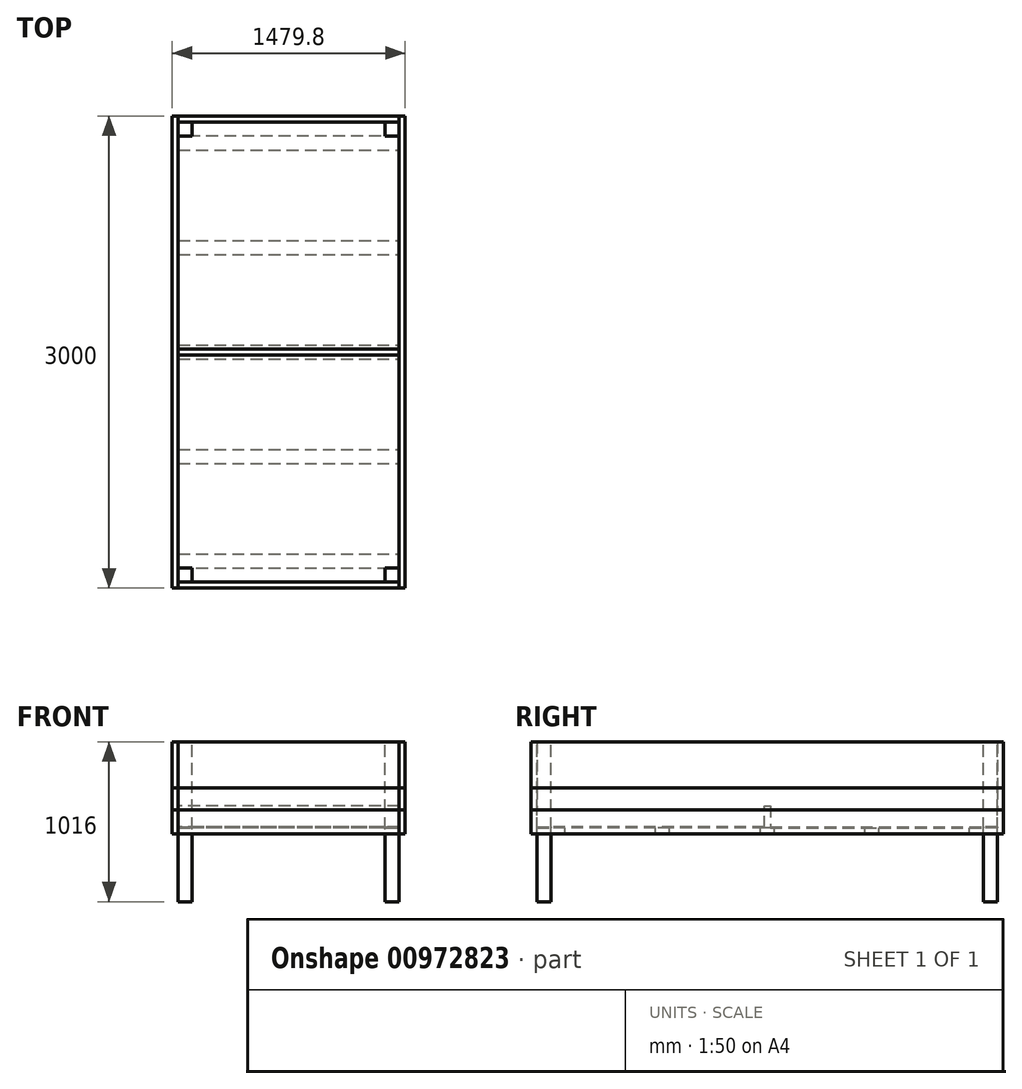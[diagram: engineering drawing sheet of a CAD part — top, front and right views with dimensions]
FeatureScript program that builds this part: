
annotation { "Feature Type Name" : "Feature", "Feature Type Description" : "" }
export const myFeature = defineFeature(function(context is Context, id is Id, definition is map)
    precondition{}
    {
        {
            var Q0;
            Q0=qCreatedBy(makeId("Top.planeOp"),FACE);
            var sketch = newSketch(context, id + "F0", { "sketchPlane" : qUnion([Q0])});
            skLineSegment(sketch, "E0.bottom", {"start": v(739.9, 1500) * mm, "end": v(-739.9, 1500) * mm});
            skLineSegment(sketch, "E0.top", {"start": v(739.9, -1500) * mm, "end": v(-739.9, -1500) * mm});
            skLineSegment(sketch, "E0.left", {"start": v(739.9, 1500) * mm, "end": v(739.9, -1500) * mm});
            skLineSegment(sketch, "E0.right", {"start": v(-739.9, 1500) * mm, "end": v(-739.9, -1500) * mm});
            skPoint(sketch, "E0.middle", {"position": v(0, 0) * mm});
            skSolve(sketch);
        }
        {
            var Q0;
            Q0=qCreatedBy(makeId("Front.planeOp"),FACE);
            var sketch = newSketch(context, id + "F1", { "sketchPlane" : qUnion([Q0])});
            skLineSegment(sketch, "E1.0", {"start": v(739.9, 0) * mm, "end": v(-739.9, 0) * mm});
            skLineSegment(sketch, "E2", {"start": v(-739.9, 0) * mm, "end": v(-739.9, -292.1) * mm});
            skLineSegment(sketch, "E3.MirrorCS", {"start": v(739.9, 0) * mm, "end": v(739.9, -292.1) * mm});
            skLineSegment(sketch, "E4", {"start": v(-739.9, -292.1) * mm, "end": v(739.9, -292.1) * mm});
            skLineSegment(sketch, "E5", {"start": v(0, 0) * mm, "end": v(0, -292.1) * mm, "construction": true});
            skLineSegment(sketch, "E6.0", {"start": v(-701.8, 0) * mm, "end": v(-701.8, -292.1) * mm});
            skLineSegment(sketch, "E7.0", {"start": v(701.8, 0) * mm, "end": v(701.8, -292.1) * mm});
            skLineSegment(sketch, "E8", {"start": v(0, 0) * mm, "end": v(0, -1016) * mm, "construction": true});
            skLineSegment(sketch, "E9", {"start": v(-739.9, -292.1) * mm, "end": v(0, -1016) * mm, "construction": true});
            skLineSegment(sketch, "E10", {"start": v(0, -1016) * mm, "end": v(-739.9, -1016) * mm, "construction": true});
            skLineSegment(sketch, "E11", {"start": v(-739.9, -1016) * mm, "end": v(-739.9, -292.1) * mm, "construction": true});
            skLineSegment(sketch, "E12", {"start": v(-739.9, -292.1) * mm, "end": v(-739.9, -431.8) * mm});
            skLineSegment(sketch, "E13", {"start": v(-739.9, -431.8) * mm, "end": v(-701.8, -431.8) * mm});
            skLineSegment(sketch, "E14", {"start": v(-701.8, -431.8) * mm, "end": v(-701.8, -292.1) * mm});
            skLineSegment(sketch, "E15.MirrorCS", {"start": v(739.9, -431.8) * mm, "end": v(701.8, -431.8) * mm});
            skLineSegment(sketch, "E16.MirrorCS", {"start": v(701.8, -431.8) * mm, "end": v(701.8, -292.1) * mm});
            skLineSegment(sketch, "E17.MirrorCS", {"start": v(739.9, -292.1) * mm, "end": v(739.9, -431.8) * mm});
            skSolve(sketch);
        }
        {
            var Q0;
            Q0=qCreatedBy(makeId("Front.planeOp"),FACE);
            var sketch = newSketch(context, id + "F2", { "sketchPlane" : qUnion([Q0])});
            skLineSegment(sketch, "E18.0", {"start": v(739.9, 0) * mm, "end": v(-739.9, 0) * mm, "construction": true});
            skLineSegment(sketch, "E19.0", {"start": v(-739.9, 0) * mm, "end": v(-739.9, -292.1) * mm, "construction": true});
            skLineSegment(sketch, "E20.0", {"start": v(-701.8, 0) * mm, "end": v(-701.8, -292.1) * mm, "construction": true});
            skLineSegment(sketch, "E21", {"start": v(-739.9, 0) * mm, "end": v(-739.9, 30) * mm});
            skLineSegment(sketch, "E22", {"start": v(-739.9, 30) * mm, "end": v(739.9, 30) * mm});
            skLineSegment(sketch, "E23", {"start": v(739.9, 30) * mm, "end": v(739.9, 0) * mm});
            skSolve(sketch);
        }
        {
            var Q0;
            {var subQ0=sQuery(id+"F1.wireOp",EDGE,"E2");Q0=makeQuery(id+"F1.imprint","IMPRINT",FACE,{"disambiguationData":[TD([[makeQuery(id+"F1.imprint","IMPRINT",EDGE,{"derivedFrom":subQ0}),1.0]])]});}
            var Q1;
            {var subQ0=sQuery(id+"F1.wireOp",EDGE,"E3.MirrorCS");Q1=makeQuery(id+"F1.imprint","IMPRINT",FACE,{"disambiguationData":[TD([[makeQuery(id+"F1.imprint","IMPRINT",EDGE,{"derivedFrom":subQ0}),-1.0]])]});}
            var Q2;
            Q2=sQuery(id+"F0.wireOp",VERTEX,"E0.top.end");
            var Q3;
            Q3=sQuery(id+"F0.wireOp",VERTEX,"E0.bottom.end");
            extrude(context, id + "F3", {"entities" : qUnion([Q0, Q1]), "endBound" : BoundingType.UP_TO_VERTEX, "depth" : 25 * mm, "endBoundEntityVertex" : qUnion([Q2]), "offsetDistance" : 25 * mm, "hasSecondDirection" : true, "secondDirectionBound" : SecondDirectionBoundingType.UP_TO_VERTEX, "secondDirectionOppositeDirection" : true, "secondDirectionDepth" : 25 * mm, "secondDirectionBoundEntityVertex" : qUnion([Q3])});
        }
        {
            var Q0;
            {var subQ0=sQuery(id+"F1.wireOp",EDGE,"E12");Q0=makeQuery(id+"F1.imprint","IMPRINT",FACE,{"disambiguationData":[TD([[makeQuery(id+"F1.imprint","IMPRINT",EDGE,{"derivedFrom":subQ0}),1.0]])]});}
            var Q1;
            Q1=makeQuery(id+"F1.imprint","IMPRINT",FACE,{"disambiguationData":[TD([[makeQuery(id+"F1.imprint","IMPRINT",EDGE,{"derivedFrom":sQuery(id+"F1.wireOp",EDGE,"E15.MirrorCS")}),-1.0]])]});
            var Q2;
            Q2=makeQuery(id+"F3.opExtrude","CAP_FACE",FACE,{"disambiguationData":[OSD([sQuery(id+"F1.wireOp",EDGE,"E1.0"),sQuery(id+"F1.wireOp",EDGE,"E2"),sQuery(id+"F1.wireOp",EDGE,"E4"),sQuery(id+"F1.wireOp",EDGE,"E6.0")])],"isStart":false});
            var Q3;
            Q3=makeQuery(id+"F3.opExtrude","CAP_FACE",FACE,{"disambiguationData":[OSD([sQuery(id+"F1.wireOp",EDGE,"E1.0"),sQuery(id+"F1.wireOp",EDGE,"E3.MirrorCS"),sQuery(id+"F1.wireOp",EDGE,"E4"),sQuery(id+"F1.wireOp",EDGE,"E7.0")])],"isStart":true});
            extrude(context, id + "F4", {"entities" : qUnion([Q0, Q1]), "endBound" : BoundingType.UP_TO_SURFACE, "depth" : 25 * mm, "endBoundEntityFace" : qUnion([Q2]), "offsetDistance" : 25 * mm, "hasSecondDirection" : true, "secondDirectionBound" : SecondDirectionBoundingType.UP_TO_SURFACE, "secondDirectionOppositeDirection" : true, "secondDirectionDepth" : 25 * mm, "secondDirectionBoundEntityFace" : qUnion([Q3])});
        }
        {
            var Q0;
            Q0=qCreatedBy(makeId("Right.planeOp"),FACE);
            var sketch = newSketch(context, id + "F5", { "sketchPlane" : qUnion([Q0])});
            skLineSegment(sketch, "E24", {"start": v(-1500, 0) * mm, "end": v(-1461.9, 0) * mm});
            skLineSegment(sketch, "E25", {"start": v(-1461.9, 0) * mm, "end": v(-1461.9, -292.1) * mm});
            skLineSegment(sketch, "E26", {"start": v(-1500, 0) * mm, "end": v(-1500, -292.1) * mm});
            skLineSegment(sketch, "E27", {"start": v(-1500, -292.1) * mm, "end": v(-1461.9, -292.1) * mm});
            skLineSegment(sketch, "E28.MirrorCS", {"start": v(1500, 0) * mm, "end": v(1461.9, 0) * mm});
            skLineSegment(sketch, "E29.MirrorCS", {"start": v(1500, -292.1) * mm, "end": v(1461.9, -292.1) * mm});
            skLineSegment(sketch, "E30.MirrorCS", {"start": v(1500, 0) * mm, "end": v(1500, -292.1) * mm});
            skLineSegment(sketch, "E31.MirrorCS", {"start": v(1461.9, 0) * mm, "end": v(1461.9, -292.1) * mm});
            skLineSegment(sketch, "E32", {"start": v(-1500, -292.1) * mm, "end": v(-1500, -431.8) * mm});
            skLineSegment(sketch, "E33", {"start": v(-1500, -431.8) * mm, "end": v(-1461.9, -431.8) * mm});
            skLineSegment(sketch, "E34", {"start": v(-1461.9, -431.8) * mm, "end": v(-1461.9, -292.1) * mm});
            skLineSegment(sketch, "E35.MirrorCS", {"start": v(1500, -431.8) * mm, "end": v(1461.9, -431.8) * mm});
            skLineSegment(sketch, "E36.MirrorCS", {"start": v(1461.9, -431.8) * mm, "end": v(1461.9, -292.1) * mm});
            skLineSegment(sketch, "E37.MirrorCS", {"start": v(1500, -292.1) * mm, "end": v(1500, -431.8) * mm});
            skLineSegment(sketch, "E38.0", {"start": v(-1500, -292.1) * mm, "end": v(1500, -292.1) * mm, "construction": true});
            skLineSegment(sketch, "E39.0", {"start": v(-1500, -431.8) * mm, "end": v(1500, -431.8) * mm, "construction": true});
            skLineSegment(sketch, "E40.0", {"start": v(0, -292.1) * mm, "end": v(0, -431.8) * mm, "construction": true});
            skLineSegment(sketch, "E41", {"start": v(0, -292.1) * mm, "end": v(-19.05, -292.1) * mm});
            skLineSegment(sketch, "E42", {"start": v(-19.05, -292.1) * mm, "end": v(-19.05, -431.8) * mm});
            skLineSegment(sketch, "E43", {"start": v(-19.05, -431.8) * mm, "end": v(19.05, -431.8) * mm});
            skLineSegment(sketch, "E44", {"start": v(19.05, -431.8) * mm, "end": v(19.05, -292.1) * mm});
            skLineSegment(sketch, "E45", {"start": v(19.05, -292.1) * mm, "end": v(0, -292.1) * mm});
            skSolve(sketch);
        }
        {
            var Q0;
            Q0=makeQuery(id+"F5.imprint","IMPRINT",FACE,{"disambiguationData":[TD([[makeQuery(id+"F5.imprint","IMPRINT",EDGE,{"derivedFrom":sQuery(id+"F5.wireOp",EDGE,"E28.MirrorCS")}),1.0]])]});
            var Q1;
            Q1=makeQuery(id+"F5.imprint","IMPRINT",FACE,{"disambiguationData":[TD([[makeQuery(id+"F5.imprint","IMPRINT",EDGE,{"derivedFrom":sQuery(id+"F5.wireOp",EDGE,"E24")}),-1.0]])]});
            var Q2;
            Q2=makeQuery(id+"F3.opExtrude","SWEPT_FACE",FACE,{"disambiguationData":[OSD([sQuery(id+"F1.wireOp",EDGE,"E7.0")])]});
            var Q3;
            Q3=makeQuery(id+"F3.opExtrude","SWEPT_FACE",FACE,{"disambiguationData":[OSD([sQuery(id+"F1.wireOp",EDGE,"E6.0")])]});
            extrude(context, id + "F6", {"entities" : qUnion([Q0, Q1]), "endBound" : BoundingType.UP_TO_SURFACE, "depth" : 25 * mm, "endBoundEntityFace" : qUnion([Q2]), "offsetDistance" : 25 * mm, "hasSecondDirection" : true, "secondDirectionBound" : SecondDirectionBoundingType.UP_TO_SURFACE, "secondDirectionOppositeDirection" : true, "secondDirectionDepth" : 25 * mm, "secondDirectionBoundEntityFace" : qUnion([Q3])});
        }
        {
            var Q0;
            Q0=makeQuery(id+"F5.imprint","IMPRINT",FACE,{"disambiguationData":[TD([[makeQuery(id+"F5.imprint","IMPRINT",EDGE,{"derivedFrom":sQuery(id+"F5.wireOp",EDGE,"E27")}),-1.0]])]});
            var Q1;
            Q1=makeQuery(id+"F5.imprint","IMPRINT",FACE,{"disambiguationData":[TD([[makeQuery(id+"F5.imprint","IMPRINT",EDGE,{"derivedFrom":sQuery(id+"F5.wireOp",EDGE,"E29.MirrorCS")}),1.0]])]});
            var Q2;
            Q2=makeQuery(id+"F5.imprint","IMPRINT",FACE,{"disambiguationData":[TD([[makeQuery(id+"F5.imprint","IMPRINT",EDGE,{"derivedFrom":sQuery(id+"F5.wireOp",EDGE,"E41")}),1.0]])]});
            var Q3;
            Q3=makeQuery(id+"F4.opExtrude","SWEPT_FACE",FACE,{"disambiguationData":[OSD([sQuery(id+"F1.wireOp",EDGE,"E16.MirrorCS")])]});
            var Q4;
            Q4=makeQuery(id+"F4.opExtrude","SWEPT_FACE",FACE,{"disambiguationData":[OSD([sQuery(id+"F1.wireOp",EDGE,"E14")])]});
            extrude(context, id + "F7", {"entities" : qUnion([Q0, Q1, Q2]), "endBound" : BoundingType.UP_TO_SURFACE, "depth" : 25 * mm, "endBoundEntityFace" : qUnion([Q3]), "offsetDistance" : 25 * mm, "hasSecondDirection" : true, "secondDirectionBound" : SecondDirectionBoundingType.UP_TO_SURFACE, "secondDirectionOppositeDirection" : true, "secondDirectionDepth" : 25 * mm, "secondDirectionBoundEntityFace" : qUnion([Q4])});
        }
        {
            var Q0;
            Q0=qCreatedBy(makeId("Top.planeOp"),FACE);
            var sketch = newSketch(context, id + "F8", { "sketchPlane" : qUnion([Q0])});
            skLineSegment(sketch, "E46.0", {"start": v(-701.8, -1500) * mm, "end": v(-701.8, 1500) * mm});
            skLineSegment(sketch, "E47.0", {"start": v(701.8, 1461.9) * mm, "end": v(-701.8, 1461.9) * mm});
            skLineSegment(sketch, "E48.0", {"start": v(-739.9, 0) * mm, "end": v(739.9, 0) * mm});
            skLineSegment(sketch, "E49", {"start": v(0, 0) * mm, "end": v(0, 1461.9) * mm, "construction": true});
            skLineSegment(sketch, "E50.bottom", {"start": v(-701.8, 1461.9) * mm, "end": v(-612.9, 1461.9) * mm});
            skLineSegment(sketch, "E50.top", {"start": v(-701.8, 1373) * mm, "end": v(-612.9, 1373) * mm});
            skLineSegment(sketch, "E50.left", {"start": v(-701.8, 1461.9) * mm, "end": v(-701.8, 1373) * mm});
            skLineSegment(sketch, "E50.right", {"start": v(-612.9, 1461.9) * mm, "end": v(-612.9, 1373) * mm});
            skLineSegment(sketch, "E51.MirrorCS", {"start": v(701.8, 1373) * mm, "end": v(612.9, 1373) * mm});
            skLineSegment(sketch, "E52.MirrorCS", {"start": v(701.8, 1461.9) * mm, "end": v(612.9, 1461.9) * mm});
            skLineSegment(sketch, "E53.MirrorCS", {"start": v(612.9, 1461.9) * mm, "end": v(612.9, 1373) * mm});
            skLineSegment(sketch, "E54.MirrorCS", {"start": v(701.8, 1461.9) * mm, "end": v(701.8, 1373) * mm});
            skLineSegment(sketch, "E55.MirrorCS", {"start": v(612.9, -1461.9) * mm, "end": v(612.9, -1373) * mm});
            skLineSegment(sketch, "E56.MirrorCS", {"start": v(701.8, -1461.9) * mm, "end": v(701.8, -1373) * mm});
            skLineSegment(sketch, "E57.MirrorCS", {"start": v(701.8, -1461.9) * mm, "end": v(612.9, -1461.9) * mm});
            skLineSegment(sketch, "E58.MirrorCS", {"start": v(701.8, -1373) * mm, "end": v(612.9, -1373) * mm});
            skLineSegment(sketch, "E59.MirrorCS", {"start": v(-612.9, -1461.9) * mm, "end": v(-612.9, -1373) * mm});
            skLineSegment(sketch, "E60.MirrorCS", {"start": v(-701.8, -1461.9) * mm, "end": v(-701.8, -1373) * mm});
            skLineSegment(sketch, "E61.MirrorCS", {"start": v(-701.8, -1373) * mm, "end": v(-612.9, -1373) * mm});
            skLineSegment(sketch, "E62.MirrorCS", {"start": v(-701.8, -1461.9) * mm, "end": v(-612.9, -1461.9) * mm});
            skSolve(sketch);
        }
        {
            var Q0;
            Q0=sQuery(id+"F1.wireOp",EDGE,"E10");
            cPlane(context, id + "F9", {"entities" : qUnion([Q0]), "cplaneType" : CPlaneType.LINE_ANGLE, "offset" : 25 * mm, "angle" : 90 * degree, "width" : 150 * mm, "height" : 150 * mm});
        }
        {
            var Q0;
            Q0=makeQuery(id+"F8.imprint","IMPRINT",FACE,{"disambiguationData":[TD([[makeQuery(id+"F8.imprint","IMPRINT",EDGE,{"derivedFrom":sQuery(id+"F8.wireOp",EDGE,"E50.bottom")}),-1.0]])]});
            var Q1;
            Q1=makeQuery(id+"F8.imprint","IMPRINT",FACE,{"disambiguationData":[TD([[makeQuery(id+"F8.imprint","IMPRINT",EDGE,{"derivedFrom":sQuery(id+"F8.wireOp",EDGE,"E51.MirrorCS")}),-1.0]])]});
            var Q2;
            Q2=makeQuery(id+"F8.imprint","IMPRINT",FACE,{"disambiguationData":[TD([[makeQuery(id+"F8.imprint","IMPRINT",EDGE,{"derivedFrom":sQuery(id+"F8.wireOp",EDGE,"E59.MirrorCS")}),1.0]])]});
            var Q3;
            Q3=makeQuery(id+"F8.imprint","IMPRINT",FACE,{"disambiguationData":[TD([[makeQuery(id+"F8.imprint","IMPRINT",EDGE,{"derivedFrom":sQuery(id+"F8.wireOp",EDGE,"E55.MirrorCS")}),-1.0]])]});
            var Q4;
            Q4=qCreatedBy(id+"F9.planeOp",FACE);
            extrude(context, id + "F10", {"entities" : qUnion([Q0, Q1, Q2, Q3]), "endBound" : BoundingType.UP_TO_SURFACE, "oppositeDirection" : true, "depth" : 40 * mm, "endBoundEntityFace" : qUnion([Q4]), "offsetDistance" : 25 * mm});
        }
        {
            var Q0;
            Q0=makeQuery(id+"F7.opExtrude","SWEPT_FACE",FACE,{"disambiguationData":[OSD([sQuery(id+"F5.wireOp",EDGE,"E33")])]});
            cPlane(context, id + "F11", {"entities" : qUnion([Q0]), "cplaneType" : CPlaneType.OFFSET, "offset" : 114.3 * mm, "width" : 152.4 * mm, "height" : 152.4 * mm});
        }
        {
            var Q0;
            Q0=qCreatedBy(id+"F11.planeOp",FACE);
            var sketch = newSketch(context, id + "F12", { "sketchPlane" : qUnion([Q0])});
            skLineSegment(sketch, "E63.0.0", {"start": v(-612.9, 1373) * mm, "end": v(-612.9, 1461.9) * mm});
            skLineSegment(sketch, "E63.0.1", {"start": v(-612.9, 1461.9) * mm, "end": v(-701.8, 1461.9) * mm});
            skLineSegment(sketch, "E63.0.2", {"start": v(-701.8, 1461.9) * mm, "end": v(-701.8, 1373) * mm});
            skLineSegment(sketch, "E63.0.3", {"start": v(-701.8, 1373) * mm, "end": v(-612.9, 1373) * mm});
            skLineSegment(sketch, "E64.0.0", {"start": v(612.9, 1461.9) * mm, "end": v(612.9, 1373) * mm});
            skLineSegment(sketch, "E64.0.1", {"start": v(612.9, 1373) * mm, "end": v(701.8, 1373) * mm});
            skLineSegment(sketch, "E64.0.2", {"start": v(701.8, 1373) * mm, "end": v(701.8, 1461.9) * mm});
            skLineSegment(sketch, "E64.0.3", {"start": v(701.8, 1461.9) * mm, "end": v(612.9, 1461.9) * mm});
            skLineSegment(sketch, "E65.0.0", {"start": v(-612.9, -1461.9) * mm, "end": v(-612.9, -1373) * mm});
            skLineSegment(sketch, "E65.0.1", {"start": v(-612.9, -1373) * mm, "end": v(-701.8, -1373) * mm});
            skLineSegment(sketch, "E65.0.2", {"start": v(-701.8, -1373) * mm, "end": v(-701.8, -1461.9) * mm});
            skLineSegment(sketch, "E65.0.3", {"start": v(-701.8, -1461.9) * mm, "end": v(-612.9, -1461.9) * mm});
            skLineSegment(sketch, "E66.0.0", {"start": v(612.9, -1461.9) * mm, "end": v(701.8, -1461.9) * mm});
            skLineSegment(sketch, "E66.0.1", {"start": v(701.8, -1461.9) * mm, "end": v(701.8, -1373) * mm});
            skLineSegment(sketch, "E66.0.2", {"start": v(701.8, -1373) * mm, "end": v(612.9, -1373) * mm});
            skLineSegment(sketch, "E66.0.3", {"start": v(612.9, -1373) * mm, "end": v(612.9, -1461.9) * mm});
            skLineSegment(sketch, "E67.0", {"start": v(701.8, -1461.9) * mm, "end": v(-701.8, -1461.9) * mm});
            skLineSegment(sketch, "E68.0", {"start": v(-701.8, 1500) * mm, "end": v(-701.8, 1373) * mm});
            skLineSegment(sketch, "E69.0", {"start": v(701.8, 1500) * mm, "end": v(701.8, 1373) * mm});
            skLineSegment(sketch, "E70.0", {"start": v(701.8, 1461.9) * mm, "end": v(-701.8, 1461.9) * mm});
            skLineSegment(sketch, "E71.0", {"start": v(701.8, 19.05) * mm, "end": v(-701.8, 19.05) * mm});
            skLineSegment(sketch, "E72.0", {"start": v(701.8, -19.05) * mm, "end": v(-701.8, -19.05) * mm});
            skLineSegment(sketch, "E73", {"start": v(-701.8, -1373) * mm, "end": v(701.8, -1373) * mm});
            skLineSegment(sketch, "E74.0", {"start": v(-739.9, 1500) * mm, "end": v(-739.9, -1500) * mm});
            skLineSegment(sketch, "E75.0", {"start": v(739.9, 1500) * mm, "end": v(739.9, -1500) * mm});
            skLineSegment(sketch, "E76", {"start": v(-739.9, 1373) * mm, "end": v(-701.8, 1373) * mm, "construction": true});
            skLineSegment(sketch, "E77", {"start": v(701.8, 1373) * mm, "end": v(739.9, 1373) * mm, "construction": true});
            skLineSegment(sketch, "E78", {"start": v(701.8, -1373) * mm, "end": v(739.9, -1373) * mm, "construction": true});
            skLineSegment(sketch, "E79", {"start": v(-701.8, -1373) * mm, "end": v(-739.9, -1373) * mm, "construction": true});
            skLineSegment(sketch, "E80", {"start": v(-739.9, 1373) * mm, "end": v(739.9, 1373) * mm});
            skLineSegment(sketch, "E81", {"start": v(-739.9, 1373) * mm, "end": v(-739.9, 1284.1) * mm});
            skLineSegment(sketch, "E82", {"start": v(-739.9, 1284.1) * mm, "end": v(739.9, 1284.1) * mm});
            skLineSegment(sketch, "E83", {"start": v(739.9, 1284.1) * mm, "end": v(739.9, 1373) * mm});
            skLineSegment(sketch, "E84.trimOffspring", {"start": v(-701.8, 1284.1) * mm, "end": v(-701.8, 708.72) * mm});
            skLineSegment(sketch, "E85.trimOffspring", {"start": v(701.8, 1284.1) * mm, "end": v(701.8, 708.72) * mm});
            skLineSegment(sketch, "E86.MirrorCS", {"start": v(-739.9, -1373) * mm, "end": v(739.9, -1373) * mm});
            skLineSegment(sketch, "E87.MirrorCS", {"start": v(-739.9, -1284.1) * mm, "end": v(739.9, -1284.1) * mm});
            skLineSegment(sketch, "E88.MirrorCS", {"start": v(739.9, -1284.1) * mm, "end": v(739.9, -1373) * mm});
            skLineSegment(sketch, "E89.MirrorCS", {"start": v(-739.9, -1373) * mm, "end": v(-739.9, -1284.1) * mm});
            skLineSegment(sketch, "E90", {"start": v(0, 1373) * mm, "end": v(0, 1284.1) * mm, "construction": true});
            skLineSegment(sketch, "E91", {"start": v(-739.9, 44.45) * mm, "end": v(739.9, 44.45) * mm});
            skLineSegment(sketch, "E92", {"start": v(-739.9, 44.45) * mm, "end": v(-739.9, -44.45) * mm});
            skLineSegment(sketch, "E93", {"start": v(-739.9, -44.45) * mm, "end": v(739.9, -44.45) * mm});
            skLineSegment(sketch, "E94", {"start": v(739.9, -44.45) * mm, "end": v(739.9, 44.45) * mm});
            skLineSegment(sketch, "E95", {"start": v(0, 44.45) * mm, "end": v(0, -44.45) * mm, "construction": true});
            skLineSegment(sketch, "E96", {"start": v(0, 1328.55) * mm, "end": v(0, 0) * mm, "construction": true});
            skLineSegment(sketch, "E97", {"start": v(0, -1373) * mm, "end": v(0, -1284.1) * mm, "construction": true});
            skLineSegment(sketch, "E98", {"start": v(0, 0) * mm, "end": v(0, -1328.55) * mm, "construction": true});
            skLineSegment(sketch, "E99", {"start": v(-739.9, 708.72) * mm, "end": v(739.9, 708.72) * mm});
            skLineSegment(sketch, "E100", {"start": v(-739.9, 708.72) * mm, "end": v(-739.9, 619.82) * mm});
            skLineSegment(sketch, "E101", {"start": v(-739.9, 619.82) * mm, "end": v(739.9, 619.82) * mm});
            skLineSegment(sketch, "E102", {"start": v(739.9, 619.82) * mm, "end": v(739.9, 708.72) * mm});
            skLineSegment(sketch, "E103", {"start": v(0, 708.72) * mm, "end": v(0, 619.82) * mm, "construction": true});
            skLineSegment(sketch, "E104", {"start": v(-739.9, -619.82) * mm, "end": v(739.9, -619.82) * mm});
            skLineSegment(sketch, "E105", {"start": v(-739.9, -619.82) * mm, "end": v(-739.9, -708.72) * mm});
            skLineSegment(sketch, "E106", {"start": v(-739.9, -708.72) * mm, "end": v(739.9, -708.72) * mm});
            skLineSegment(sketch, "E107", {"start": v(739.9, -708.72) * mm, "end": v(739.9, -619.82) * mm});
            skLineSegment(sketch, "E108", {"start": v(0, -619.82) * mm, "end": v(0, -708.72) * mm, "construction": true});
            skLineSegment(sketch, "E109.trimOffspring", {"start": v(-701.8, 619.82) * mm, "end": v(-701.8, 44.45) * mm});
            skLineSegment(sketch, "E110.trimOffspring", {"start": v(701.8, 619.82) * mm, "end": v(701.8, 44.45) * mm});
            skLineSegment(sketch, "E111.trimOffspring", {"start": v(701.8, -708.72) * mm, "end": v(701.8, -1284.1) * mm});
            skLineSegment(sketch, "E112.trimOffspring", {"start": v(-701.8, -708.72) * mm, "end": v(-701.8, -1284.1) * mm});
            skLineSegment(sketch, "E113.trimOffspring", {"start": v(-701.8, -1373) * mm, "end": v(-701.8, -1500) * mm});
            skLineSegment(sketch, "E114.trimOffspring", {"start": v(701.8, -1373) * mm, "end": v(701.8, -1500) * mm});
            skLineSegment(sketch, "E115.trimOffspring", {"start": v(701.8, -44.45) * mm, "end": v(701.8, -619.82) * mm});
            skLineSegment(sketch, "E116.trimOffspring", {"start": v(-701.8, 19.05) * mm, "end": v(-701.8, -19.05) * mm});
            skLineSegment(sketch, "E117.trimOffspring", {"start": v(-701.8, -44.45) * mm, "end": v(-701.8, -619.82) * mm});
            skLineSegment(sketch, "E118", {"start": v(701.8, 19.05) * mm, "end": v(701.8, -19.05) * mm});
            skLineSegment(sketch, "E119", {"start": v(701.8, 1373) * mm, "end": v(701.8, 1284.1) * mm});
            skLineSegment(sketch, "E120", {"start": v(701.8, 708.72) * mm, "end": v(701.8, 619.82) * mm});
            skLineSegment(sketch, "E121", {"start": v(701.8, 44.45) * mm, "end": v(701.8, -44.45) * mm});
            skLineSegment(sketch, "E122", {"start": v(701.8, -619.82) * mm, "end": v(701.8, -708.72) * mm});
            skLineSegment(sketch, "E123", {"start": v(701.8, -1284.1) * mm, "end": v(701.8, -1373) * mm});
            skLineSegment(sketch, "E124", {"start": v(-701.8, -1373) * mm, "end": v(-701.8, -1284.1) * mm});
            skLineSegment(sketch, "E125", {"start": v(-701.8, -708.72) * mm, "end": v(-701.8, -619.82) * mm});
            skLineSegment(sketch, "E126", {"start": v(-701.8, -44.45) * mm, "end": v(-701.8, 44.45) * mm});
            skLineSegment(sketch, "E127", {"start": v(-701.8, 619.82) * mm, "end": v(-701.8, 708.72) * mm});
            skLineSegment(sketch, "E128", {"start": v(-701.8, 1284.1) * mm, "end": v(-701.8, 1373) * mm});
            skSolve(sketch);
        }
        {
            var Q0;
            {var subQ5=sQuery(id+"F12.wireOp",EDGE,"E63.0.0");Q0=makeQuery(id+"F12.imprint","IMPRINT",FACE,{"disambiguationData":[TD([[makeQuery(id+"F12.imprint","IMPRINT",EDGE,{"derivedFrom":subQ5}),-1.0]])]});}
            var Q1;
            {var subQ3=sQuery(id+"F12.wireOp",EDGE,"E65.0.0");Q1=makeQuery(id+"F12.imprint","IMPRINT",FACE,{"disambiguationData":[TD([[makeQuery(id+"F12.imprint","IMPRINT",EDGE,{"derivedFrom":subQ3}),-1.0]])]});}
            var Q2;
            {var subQ2=sQuery(id+"F12.wireOp",EDGE,"E119");Q2=makeQuery(id+"F12.imprint","IMPRINT",FACE,{"disambiguationData":[TD([[makeQuery(id+"F12.imprint","IMPRINT",EDGE,{"derivedFrom":subQ2}),-1.0]])]});}
            var Q3;
            {var subQ0=sQuery(id+"F12.wireOp",EDGE,"E84.trimOffspring");Q3=makeQuery(id+"F12.imprint","IMPRINT",FACE,{"disambiguationData":[TD([[makeQuery(id+"F12.imprint","IMPRINT",EDGE,{"derivedFrom":subQ0}),1.0]])]});}
            var Q4;
            {var subQ2=sQuery(id+"F12.wireOp",EDGE,"E120");Q4=makeQuery(id+"F12.imprint","IMPRINT",FACE,{"disambiguationData":[TD([[makeQuery(id+"F12.imprint","IMPRINT",EDGE,{"derivedFrom":subQ2}),-1.0]])]});}
            var Q5;
            {var subQ0=sQuery(id+"F12.wireOp",EDGE,"E109.trimOffspring");Q5=makeQuery(id+"F12.imprint","IMPRINT",FACE,{"disambiguationData":[TD([[makeQuery(id+"F12.imprint","IMPRINT",EDGE,{"derivedFrom":subQ0}),1.0]])]});}
            var Q6;
            {var subQ0=sQuery(id+"F12.wireOp",EDGE,"E71.0");Q6=makeQuery(id+"F12.imprint","IMPRINT",FACE,{"disambiguationData":[TD([[makeQuery(id+"F12.imprint","IMPRINT",EDGE,{"derivedFrom":subQ0}),-1.0]])]});}
            var Q7;
            {var subQ0=sQuery(id+"F12.wireOp",EDGE,"E115.trimOffspring");Q7=makeQuery(id+"F12.imprint","IMPRINT",FACE,{"disambiguationData":[TD([[makeQuery(id+"F12.imprint","IMPRINT",EDGE,{"derivedFrom":subQ0}),-1.0]])]});}
            var Q8;
            {var subQ2=sQuery(id+"F12.wireOp",EDGE,"E123");Q8=makeQuery(id+"F12.imprint","IMPRINT",FACE,{"disambiguationData":[TD([[makeQuery(id+"F12.imprint","IMPRINT",EDGE,{"derivedFrom":subQ2}),-1.0]])]});}
            var Q9;
            {var subQ0=sQuery(id+"F12.wireOp",EDGE,"E122");Q9=makeQuery(id+"F12.imprint","IMPRINT",FACE,{"disambiguationData":[TD([[makeQuery(id+"F12.imprint","IMPRINT",EDGE,{"derivedFrom":subQ0}),-1.0]])]});}
            var Q10;
            {var subQ0=sQuery(id+"F12.wireOp",EDGE,"E111.trimOffspring");Q10=makeQuery(id+"F12.imprint","IMPRINT",FACE,{"disambiguationData":[TD([[makeQuery(id+"F12.imprint","IMPRINT",EDGE,{"derivedFrom":subQ0}),-1.0]])]});}
            var Q11;
            {var subQ0=sQuery(id+"F12.wireOp",EDGE,"E72.0");Q11=makeQuery(id+"F12.imprint","IMPRINT",FACE,{"disambiguationData":[TD([[makeQuery(id+"F12.imprint","IMPRINT",EDGE,{"derivedFrom":subQ0}),1.0]])]});}
            extrude(context, id + "F13", {"entities" : qUnion([Q0, Q1, Q2, Q3, Q4, Q5, Q6, Q7, Q8, Q9, Q10, Q11]), "oppositeDirection" : true, "depth" : 6.35 * mm, "offsetDistance" : 25.4 * mm});
        }
        {
            var Q0;
            Q0=makeQuery(id+"F12.imprint","IMPRINT",FACE,{"disambiguationData":[TD([[makeQuery(id+"F12.imprint","IMPRINT",EDGE,{"derivedFrom":sQuery(id+"F12.wireOp",EDGE,"E71.0")}),-1.0]])]});
            var Q1;
            Q1=makeQuery(id+"F12.imprint","IMPRINT",FACE,{"disambiguationData":[TD([[makeQuery(id+"F12.imprint","IMPRINT",EDGE,{"derivedFrom":sQuery(id+"F12.wireOp",EDGE,"E71.0")}),1.0]])]});
            var Q2;
            {var subQ2=sQuery(id+"F12.wireOp",EDGE,"E119");Q2=makeQuery(id+"F12.imprint","IMPRINT",FACE,{"disambiguationData":[TD([[makeQuery(id+"F12.imprint","IMPRINT",EDGE,{"derivedFrom":subQ2}),-1.0]])]});}
            var Q3;
            {var subQ2=sQuery(id+"F12.wireOp",EDGE,"E120");Q3=makeQuery(id+"F12.imprint","IMPRINT",FACE,{"disambiguationData":[TD([[makeQuery(id+"F12.imprint","IMPRINT",EDGE,{"derivedFrom":subQ2}),-1.0]])]});}
            var Q4;
            {var subQ0=sQuery(id+"F12.wireOp",EDGE,"E72.0");Q4=makeQuery(id+"F12.imprint","IMPRINT",FACE,{"disambiguationData":[TD([[makeQuery(id+"F12.imprint","IMPRINT",EDGE,{"derivedFrom":subQ0}),1.0]])]});}
            var Q5;
            {var subQ0=sQuery(id+"F12.wireOp",EDGE,"E122");Q5=makeQuery(id+"F12.imprint","IMPRINT",FACE,{"disambiguationData":[TD([[makeQuery(id+"F12.imprint","IMPRINT",EDGE,{"derivedFrom":subQ0}),-1.0]])]});}
            var Q6;
            {var subQ2=sQuery(id+"F12.wireOp",EDGE,"E123");Q6=makeQuery(id+"F12.imprint","IMPRINT",FACE,{"disambiguationData":[TD([[makeQuery(id+"F12.imprint","IMPRINT",EDGE,{"derivedFrom":subQ2}),-1.0]])]});}
            extrude(context, id + "F14", {"entities" : qUnion([Q0, Q1, Q2, Q3, Q4, Q5, Q6]), "depth" : 38.1 * mm, "offsetDistance" : 25.4 * mm});
        }
        {
            var Q0;
            Q0=makeQuery(id+"F7.opExtrude","SWEPT_FACE",FACE,{"disambiguationData":[OSD([sQuery(id+"F5.wireOp",EDGE,"E33")])]});
            var Q1;
            Q1=makeQuery(id+"F7.opExtrude","SWEPT_FACE",FACE,{"disambiguationData":[OSD([sQuery(id+"F5.wireOp",EDGE,"E35.MirrorCS")])]});
            var Q2;
            Q2=makeQuery(id+"F4.opExtrude","SWEPT_FACE",FACE,{"disambiguationData":[OSD([sQuery(id+"F1.wireOp",EDGE,"E13")])]});
            var Q3;
            Q3=makeQuery(id+"F4.opExtrude","SWEPT_FACE",FACE,{"disambiguationData":[OSD([sQuery(id+"F1.wireOp",EDGE,"E15.MirrorCS")])]});
            extrude(context, id + "F15", {"entities" : qUnion([Q0, Q1, Q2, Q3]), "depth" : 152.4 * mm, "offsetDistance" : 25.4 * mm});
        }
        {
            var Q0;
            Q0=makeQuery(id+"F7.opExtrude","SWEPT_BODY",BODY,{"disambiguationData":[OSD([sQuery(id+"F5.wireOp",EDGE,"E41"),sQuery(id+"F5.wireOp",EDGE,"E42"),sQuery(id+"F5.wireOp",EDGE,"E43"),sQuery(id+"F5.wireOp",EDGE,"E44"),sQuery(id+"F5.wireOp",EDGE,"E45")])]});
            transform(context, id + "F16", {"entities" : qUnion([Q0]), "transformType" : TransformType.TRANSLATION_3D, "dx" : 0 * mm, "dy" : 0 * mm, "dz" : -114.3 * mm, "makeCopy" : false});
        }
    });
